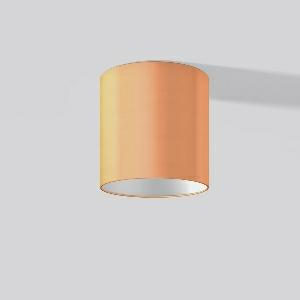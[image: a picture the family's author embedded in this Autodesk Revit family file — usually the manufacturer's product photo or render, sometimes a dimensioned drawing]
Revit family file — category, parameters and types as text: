
# Revit family: toledo_flatliner_901634_002_76_d587
name_source: partatom
category: Lighting Fixtures
units: mm (PartAtom-declared; Revit-internal decimal feet)

## family parameters
Cut with Voids When Loaded = No
Host = Face
Light Source = No
Part Type = Normal
Room Calculation Point = No
Round Connector Dimension = Use Diameter
Shared = No

## types (1)
- 982302.002 (1 x LED Modul 830, 1700 lm, 3000)
    Apparent Load = 22 VA
    CIE Flux Codes = 50 82 97 99 100
    Color Rendering = 80
    Color Temperature = 3000
    Default Elevation = 1800 mm
    Description = Series: TOLEDO FLATLINER
Decorative ceiling luminaire for interior decoration. Base luminaire prepared for the installation of fabric lampshade. Cylinder housing sheet steel, powder-coated. Housing: die cast aluminium and sheet steel, powder-coated. Bezel ring: die-cast aluminium, powder-coated. Lightguide and diffuser made of non-yellowing plastic (PMMA) opal matt. Modular design: With the basic luminaire, a square or cylindrical fabric lampshade must always be ordered separately. Fabric lampshades can be fitted to the basic luminaire without tools. Order satin finish diffuser as separate accessory. 
Colour: white
Diameter: 330 mm
Height: 70 mm
Lamp: LED
Socket: without socket
Colour temperature: 3000K
Colour rendering index (CRI): 80
System power: 22 W
Rated luminous flux: 1700 lm
Luminous efficiency: 77 lm/W
Control gear: Converter, dimmable, DALI
Protection class: II
Type of protection: IP 40
    Height = 70 mm
    Lamp = 1 x LED Modul 830
    Lamp Light Flux = 1700 lm
    Lamp count = 1
    Length = 330 mm
    Lifetime = 50000 h
    Luminous efficacy = 77 lm/W
    Manufacturer = RZB
    ModVariant = No
    Model = 901634.002.76
    Mounting Place = Ceiling
    Mounting Type = Surface mounted
    Number of Poles = 1
    OnlyDefault = Yes
    Power Factor = 1
    Product Name = TOLEDO FLATLINER
    Product group = Surface mounted ceiling Fabric lampshade luminaires
    ProductGroupID = 313
    Protection Class = Protection class II
    Protection Degree = IP 40
    RLX_Detail_Level = 1
    RLX_Emergency_Light_Flux = 0 lm
    RLX_Emergency_Type = 0
    RLX_Emergency_Type_DB = No
    RlxData = <blob elided: 62725 chars, md5=9e271d0a>
    Socket = socket
    Standby Power = 0 W
    System Light Flux = 1700 lm
    System Power = 22 W
    Type Image = toledo_flatliner_anbau_rund_orange_odeckel.jpg
    URL = http://relux.com
    VarID = 982302_002_891e
    Voltage = 230 V
    Voltage Range = 220-240 V
    Weight = 0.00 kg
    Width = 0 mm  [stored 0 ft]

note: [stored X ft] marks values corroborated as IEEE doubles in the binary element streams (Revit-internal decimal feet)

## geometry (parser evidence)
native form markers: Blend x4, Sweep x11
no freeform markers — native parametric forms only
